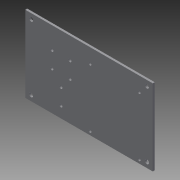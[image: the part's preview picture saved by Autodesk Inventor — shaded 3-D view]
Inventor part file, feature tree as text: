
AUTODESK INVENTOR PART (.ipt)
format: ipt  version: 2014 (Build 180170000, 170)  size: 133,632 bytes
history: native  units: mm
features: extrude x3, sketch x3
ambient origin geometry x8: Origin, YZ Plane, XZ Plane, XY Plane, X Axis, Y Axis, Z Axis, Center Point
bodies: Solid1 (feature_tree)
feature tree (6):
  extrude  "Extrusion1"  Depth=127.0mm
  extrude  "Extrusion2"  Depth=2.0mm
  extrude  "Extrusion3"  Depth=10.0mm
  sketch  "Sketch1"  dims[d0=76.0mm d1=127.0mm]
  sketch  "Sketch2"  dims[d2=2.0mm d3=0.0mm d5=32.6mm]
  sketch  "Sketch3"  dims[d6=57.7mm d7=4.0mm d8=10.0mm d9=0.0mm d10=93.0mm d12=51.0mm d13=10.0mm d14=56.0mm d15=85.0mm d16=27.0mm d17=3.0mm d18=20.0mm d20=55.0mm d21=10.0mm d23=10.0mm d25=0.0mm d27=2.75mm d29=20.0mm d31=58.0mm d32=20.0mm d34=49.0mm d37=10.0mm d38=0.0mm d39=3.5mm d41=3.5mm d42=3.0mm d43=8.98mm d44=27.5mm d45=3.0mm d46=55.0mm d47=3.0mm d48=27.5mm d49=11.0mm d50=8.98mm d51=8.98mm d52=3.0mm]
